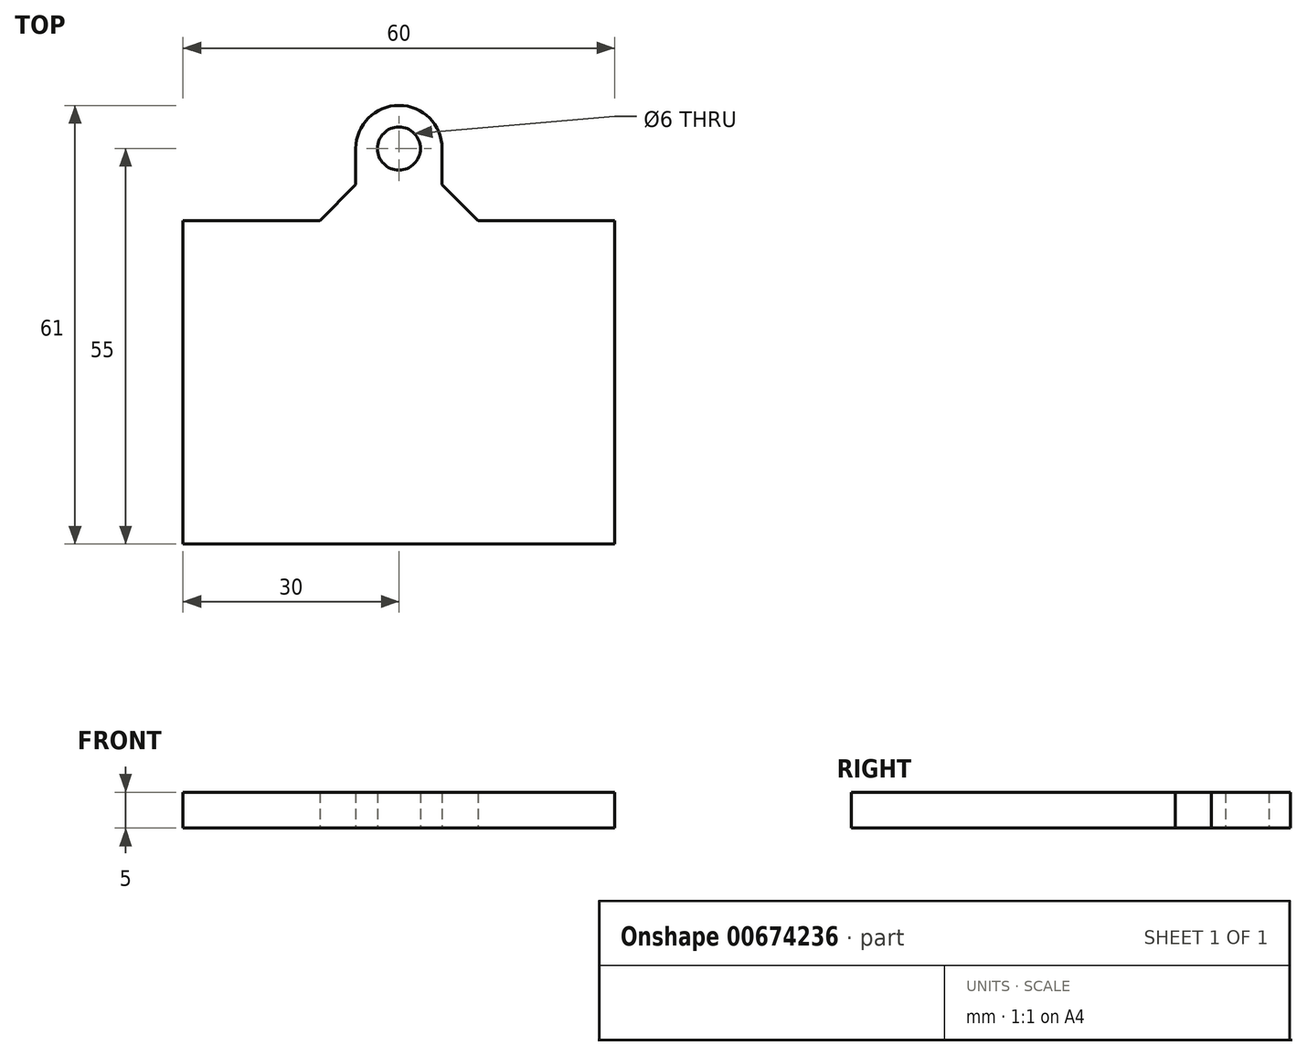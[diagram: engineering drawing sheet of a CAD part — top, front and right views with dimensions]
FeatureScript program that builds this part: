
annotation { "Feature Type Name" : "Feature", "Feature Type Description" : "" }
export const myFeature = defineFeature(function(context is Context, id is Id, definition is map)
    precondition{}
    {
        {
            var Q0;
            Q0=qCreatedBy(makeId("Top.planeOp"),FACE);
            var sketch = newSketch(context, id + "F0", { "sketchPlane" : qUnion([Q0])});
            skLineSegment(sketch, "E0.bottom", {"start": v(30, 22.5) * mm, "end": v(-30, 22.5) * mm});
            skLineSegment(sketch, "E0.top", {"start": v(30, -22.5) * mm, "end": v(-30, -22.5) * mm});
            skLineSegment(sketch, "E0.left", {"start": v(30, 22.5) * mm, "end": v(30, -22.5) * mm});
            skLineSegment(sketch, "E0.right", {"start": v(-30, 22.5) * mm, "end": v(-30, -22.5) * mm});
            skCircle(sketch, "E1", {"center": v(0, 32.5) * mm, "radius": 3 * mm});
            skArc(sketch, "E2.0", {"start": v(6, 32.5) * mm, "mid": v(0, 38.5) * mm, "end": v(-6, 32.5) * mm});
            skLineSegment(sketch, "E3", {"start": v(-6, 32.5) * mm, "end": v(6, 32.5) * mm, "construction": true});
            skLineSegment(sketch, "E4", {"start": v(-6, 32.5) * mm, "end": v(-6, 22.5) * mm});
            skLineSegment(sketch, "E5", {"start": v(6, 32.5) * mm, "end": v(6, 22.5) * mm});
            skLineSegment(sketch, "E6", {"start": v(-11, 22.5) * mm, "end": v(-6, 27.5) * mm});
            skLineSegment(sketch, "E7", {"start": v(0, 0) * mm, "end": v(0, 56.18) * mm, "construction": true});
            skLineSegment(sketch, "E8.MirrorCS", {"start": v(11, 22.5) * mm, "end": v(6, 27.5) * mm});
            skLineSegment(sketch, "E9", {"start": v(-30, -22.5) * mm, "end": v(30, 22.5) * mm, "construction": true});
            skPoint(sketch, "E10", {"position": v(0, -22.5) * mm});
            skSolve(sketch);
        }
        {
            var Q0;
            {var subQ0=sQuery(id+"F0.wireOp",EDGE,"E0.bottom");var subQ5=sQuery(id+"F0.wireOp",EDGE,"E0.left");var subQ6=makeQuery(id+"F0.imprint","INTERSECT",VERTEX,{"derivedFrom":[subQ0,subQ5]});Q0=makeQuery(id+"F0.imprint","IMPRINT",FACE,{"disambiguationData":[TD([[makeQuery(id+"F0.imprint","IMPRINT",EDGE,{"disambiguationData":[TD([[subQ6,-1.0]])],"derivedFrom":subQ0}),1.0]])]});}
            var Q1;
            {var subQ3=sQuery(id+"F0.wireOp",EDGE,"E6");Q1=makeQuery(id+"F0.imprint","IMPRINT",FACE,{"disambiguationData":[TD([[makeQuery(id+"F0.imprint","IMPRINT",EDGE,{"derivedFrom":subQ3}),-1.0]])]});}
            var Q2;
            Q2=makeQuery(id+"F0.imprint","IMPRINT",FACE,{"disambiguationData":[TD([[makeQuery(id+"F0.imprint","IMPRINT",EDGE,{"derivedFrom":sQuery(id+"F0.wireOp",EDGE,"E1")}),-1.0]])]});
            var Q3;
            {var subQ3=sQuery(id+"F0.wireOp",EDGE,"E8.MirrorCS");Q3=makeQuery(id+"F0.imprint","IMPRINT",FACE,{"disambiguationData":[TD([[makeQuery(id+"F0.imprint","IMPRINT",EDGE,{"derivedFrom":subQ3}),1.0]])]});}
            extrude(context, id + "F1", {"entities" : qUnion([Q0, Q1, Q2, Q3]), "depth" : 5 * mm, "offsetDistance" : 25 * mm});
        }
    });
